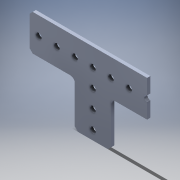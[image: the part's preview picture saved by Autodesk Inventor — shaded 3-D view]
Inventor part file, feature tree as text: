
AUTODESK INVENTOR PART (.ipt)
format: ipt  version: 2017 (Build 210142000, 142)  size: 143,360 bytes
history: native  units: in
note: dims shown in document units (in); Inventor stores cm internally (conversion verified against a paired STEP export)
features: extrude x1, sketch x1, fillet x1
ambient origin geometry x8: Origin, YZ Plane, XZ Plane, XY Plane, X Axis, Y Axis, Z Axis, Center Point
bodies: Solid1 (feature_tree)
feature tree (3):
  extrude  "Extrusion1"  [1 undecoded]
  sketch  "Sketch1"  dims[d1=1.0in d2=0.0in]
  fillet  "Fillet1"  [1 undecoded]
note: 2 required parameter values undecoded (feature->parameter linkage not recoverable at this tier; creation-order binding heuristic only, values carry confidence <= 0.55)
